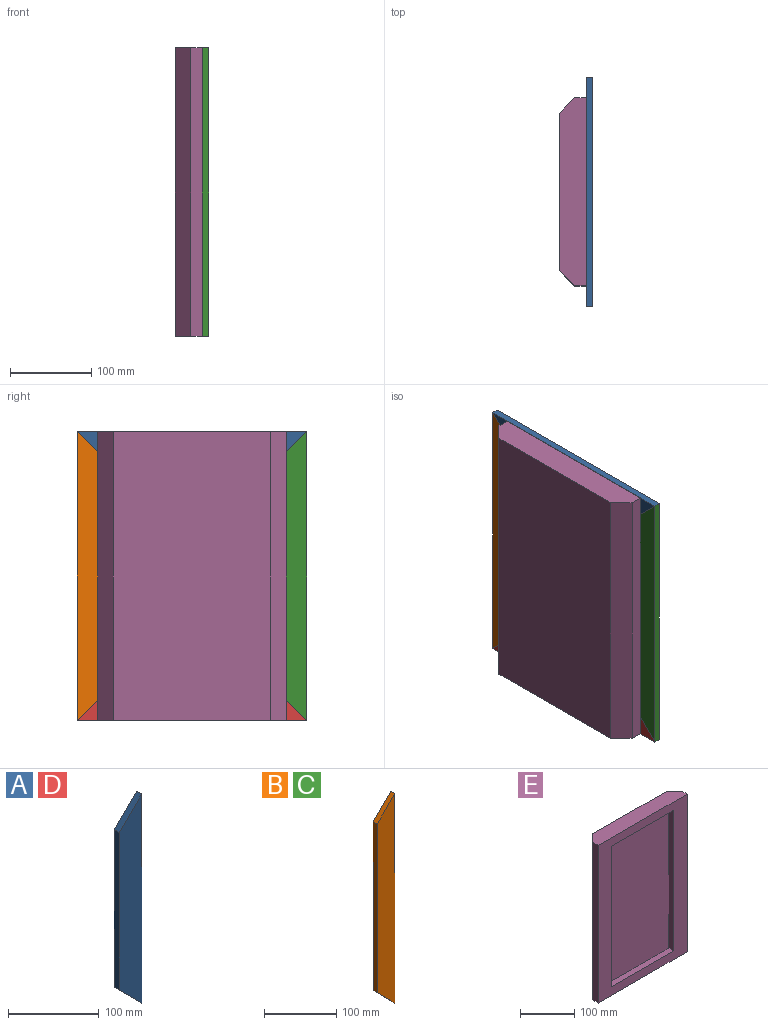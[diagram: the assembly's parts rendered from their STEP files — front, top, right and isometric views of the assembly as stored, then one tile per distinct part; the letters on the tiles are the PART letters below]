
ASSEMBLY  parts=5 mates=6
PART A: 6 faces, bbox 34.9x7.9x282.6 mm
  f0: plane 282.58x7.94mm, normal (1,0,0), area 2242.9mm2, adj f1,f3,f4,f5
  f1: plane 34.93x34.93mm, normal (-0.71,0,0.71), area 392mm2, adj f0,f2,f4,f5
  f2: plane 212.73x7.94mm, normal (-1,0,0), area 1688.5mm2, adj f1,f3,f4,f5
  f3: plane 34.93x34.93mm, normal (-0.71,0,-0.71), area 392mm2, adj f0,f2,f4,f5
  f4: plane 282.58x34.93mm, normal (0,-1,0), area 8649.2mm2, adj f0,f1,f2,f3
  f5: plane 282.58x34.93mm, normal (0,1,0), area 8649.2mm2, adj f0,f1,f2,f3
PART B: 6 faces, bbox 34.9x7.9x355.6 mm
  f0: plane 355.6x7.94mm, normal (1,0,0), area 2822.6mm2, adj f1,f3,f4,f5
  f1: plane 34.93x34.93mm, normal (-0.71,0,0.71), area 392mm2, adj f0,f2,f4,f5
  f2: plane 285.75x7.94mm, normal (-1,0,0), area 2268.1mm2, adj f1,f3,f4,f5
  f3: plane 34.93x34.93mm, normal (-0.71,0,-0.71), area 392mm2, adj f0,f2,f4,f5
  f4: plane 355.6x34.93mm, normal (0,-1,0), area 11199.6mm2, adj f0,f1,f2,f3
  f5: plane 355.6x34.93mm, normal (0,1,0), area 11199.6mm2, adj f0,f1,f2,f3
PART C: same geometry as B
PART D: same geometry as A
PART E: 13 faces, bbox 231.8x33.3x355.6 mm
  f0: plane 161.93x12.7mm, normal (0,0,-1), area 2056.4mm2, adj f1,f7,f8,f10
  f1: plane 317.5x12.7mm, normal (-1,0,0), area 4032.3mm2, adj f0,f2,f8,f10
  f2: plane 161.93x12.7mm, normal (0,0,1), area 2056.4mm2, adj f1,f7,f8,f10
  f3: plane 355.6x14.29mm, normal (1,0,0), area 5080.6mm2, adj f4,f6,f8,f11
  f4: plane 231.78x33.34mm, normal (0,0,1), area 7363.9mm2, adj f3,f5,f8,f9,f11,f12
  f5: plane 355.6x14.29mm, normal (-1,0,0), area 5080.6mm2, adj f4,f6,f8,f12
  f6: plane 231.78x33.34mm, normal (0,0,-1), area 7363.9mm2, adj f3,f5,f8,f9,f11,f12
  f7: plane 317.5x12.7mm, normal (1,0,0), area 4032.3mm2, adj f0,f2,f8,f10
  f8: plane 355.6x231.78mm, normal (0,-1,0), area 31008mm2, adj f0,f1,f2,f3,f4,f5,f6,f7
  f9: plane 355.6x193.68mm, normal (0,1,0), area 68870.8mm2, adj f4,f6,f11,f12
  f10: plane 317.5x161.93mm, normal (0,-1,0), area 51411.2mm2, adj f0,f1,f2,f7
  f11: plane 355.6x19.05mm, normal (0.71,0.71,0), area 9580.1mm2, adj f3,f4,f6,f9
  f12: plane 355.6x19.05mm, normal (-0.71,0.71,0), area 9580.1mm2, adj f4,f5,f6,f9
PLACE A rot(axis=(0.58,-0.58,0.58),120deg) t=(0,115.89,338.14)mm
PLACE B rot(axis=(0.71,0.71,0),180deg) t=(7.94,239.71,177.8)mm
PLACE C rot(axis=(0.71,-0.71,0),180deg) t=(0,-7.94,177.8)mm
PLACE D rot(axis=(0.58,0.58,-0.58),120deg) t=(7.94,115.89,17.46)mm
PLACE E rot(axis=(0,0,1),90deg) t=(-33.34,115.89,177.8)mm
MATE fastened C.f3 <-> A.f1  axis (0,0.71,0.71) through (3.97,-7.94,338.14)mm
MATE fastened C.f1 <-> D.f1  axis (0,0.71,-0.71) through (3.97,-7.94,17.46)mm
MATE fastened D.f3 <-> B.f1  axis (0,0.71,0.71) through (3.97,239.71,17.46)mm
MATE parallel E.f5 <-> B.f0  axis (0,-1,0) through (-7.14,0,177.8)mm
MATE fastened E.f4 <-> A.f0  axis (0,0,1) through (0,115.89,355.6)mm
MATE planar B.f4 <-> E.f8  axis (-1,0,0) through (0,240.35,177.8)mm
